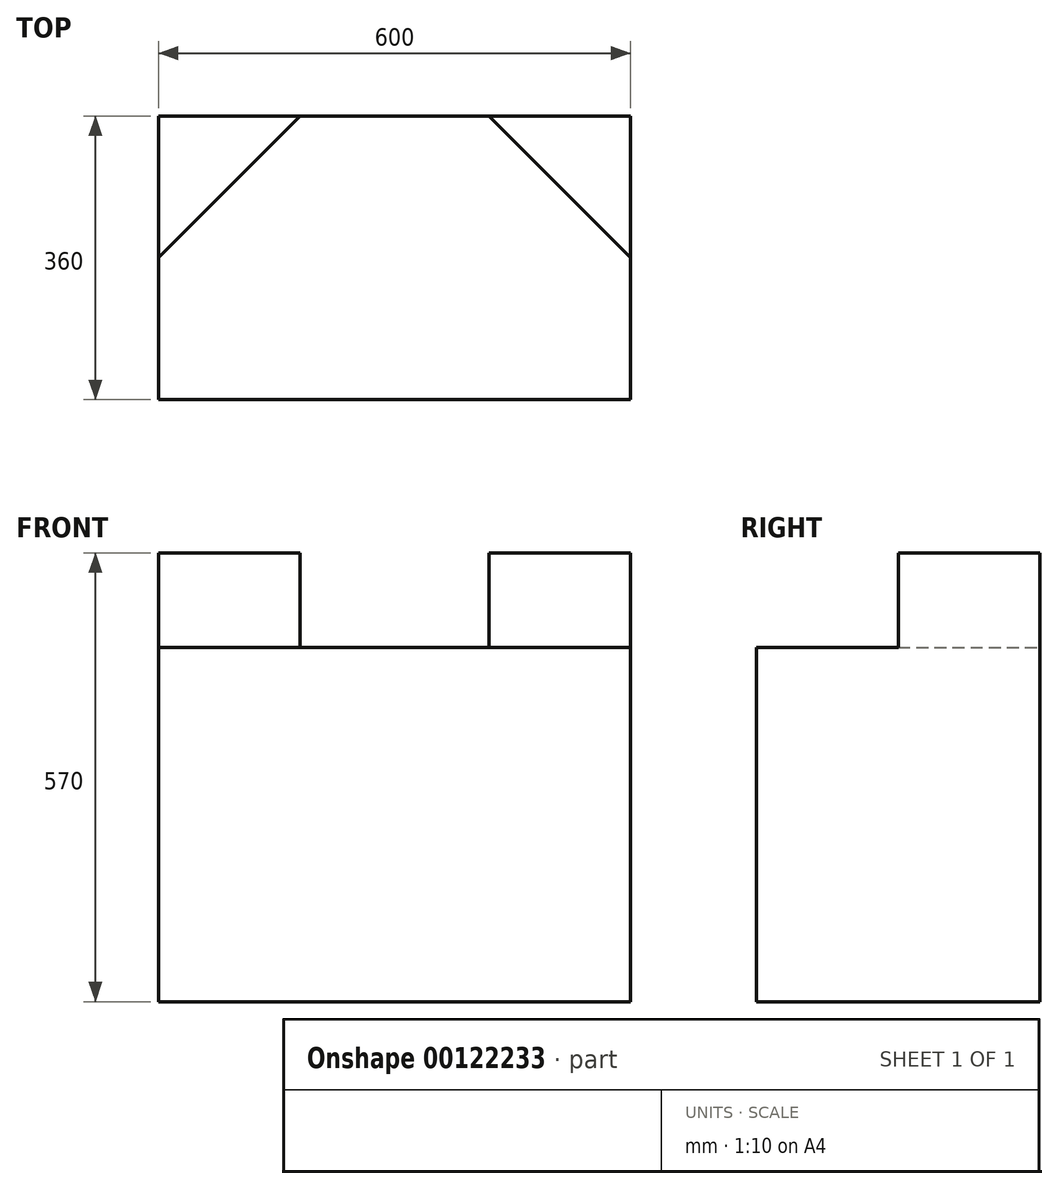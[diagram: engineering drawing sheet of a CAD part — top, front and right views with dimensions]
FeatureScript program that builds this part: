
annotation { "Feature Type Name" : "Feature", "Feature Type Description" : "" }
export const myFeature = defineFeature(function(context is Context, id is Id, definition is map)
    precondition{}
    {
        {
            var Q0;
            Q0=qCreatedBy(makeId("Front.planeOp"),FACE);
            var sketch = newSketch(context, id + "F0", { "sketchPlane" : qUnion([Q0])});
            skLineSegment(sketch, "E0.bottom", {"start": v(-300, -285) * mm, "end": v(300, -285) * mm});
            skLineSegment(sketch, "E0.top", {"start": v(-300, 285) * mm, "end": v(300, 285) * mm});
            skLineSegment(sketch, "E0.left", {"start": v(-300, -285) * mm, "end": v(-300, 285) * mm});
            skLineSegment(sketch, "E0.right", {"start": v(300, -285) * mm, "end": v(300, 285) * mm});
            skPoint(sketch, "E0.middle", {"position": v(0, 0) * mm});
            skSolve(sketch);
        }
        {
            var Q0;
            Q0 = qSketchRegion(id + "F0", true);
            extrude(context, id + "F1", {"entities" : qUnion([Q0]), "depth" : 360 * mm});
        }
        {
            var Q0;
            Q0=makeQuery(id+"F1.opExtrude","SWEPT_FACE",FACE,{"disambiguationData":[OSD([sQuery(id+"F0.wireOp",EDGE,"E0.top")])]});
            var sketch = newSketch(context, id + "F2", { "sketchPlane" : qUnion([Q0])});
            skLineSegment(sketch, "E1", {"start": v(-300, -360) * mm, "end": v(-300, -180) * mm});
            skLineSegment(sketch, "E2", {"start": v(-300, -180) * mm, "end": v(-120, 0) * mm});
            skLineSegment(sketch, "E3", {"start": v(-120, 0) * mm, "end": v(120, 0) * mm});
            skLineSegment(sketch, "E4", {"start": v(120, 0) * mm, "end": v(300, -180) * mm});
            skLineSegment(sketch, "E5", {"start": v(300, -180) * mm, "end": v(300, -360) * mm});
            skLineSegment(sketch, "E6", {"start": v(300, -360) * mm, "end": v(-300, -360) * mm});
            skPoint(sketch, "E7", {"position": v(0, 0) * mm});
            skSolve(sketch);
        }
        {
            var Q0;
            Q0 = qSketchRegion(id + "F2", true);
            extrude(context, id + "F3", {"entities" : qUnion([Q0]), "operationType" : NewBodyOperationType.REMOVE, "oppositeDirection" : true, "depth" : 120 * mm});
        }
    });
